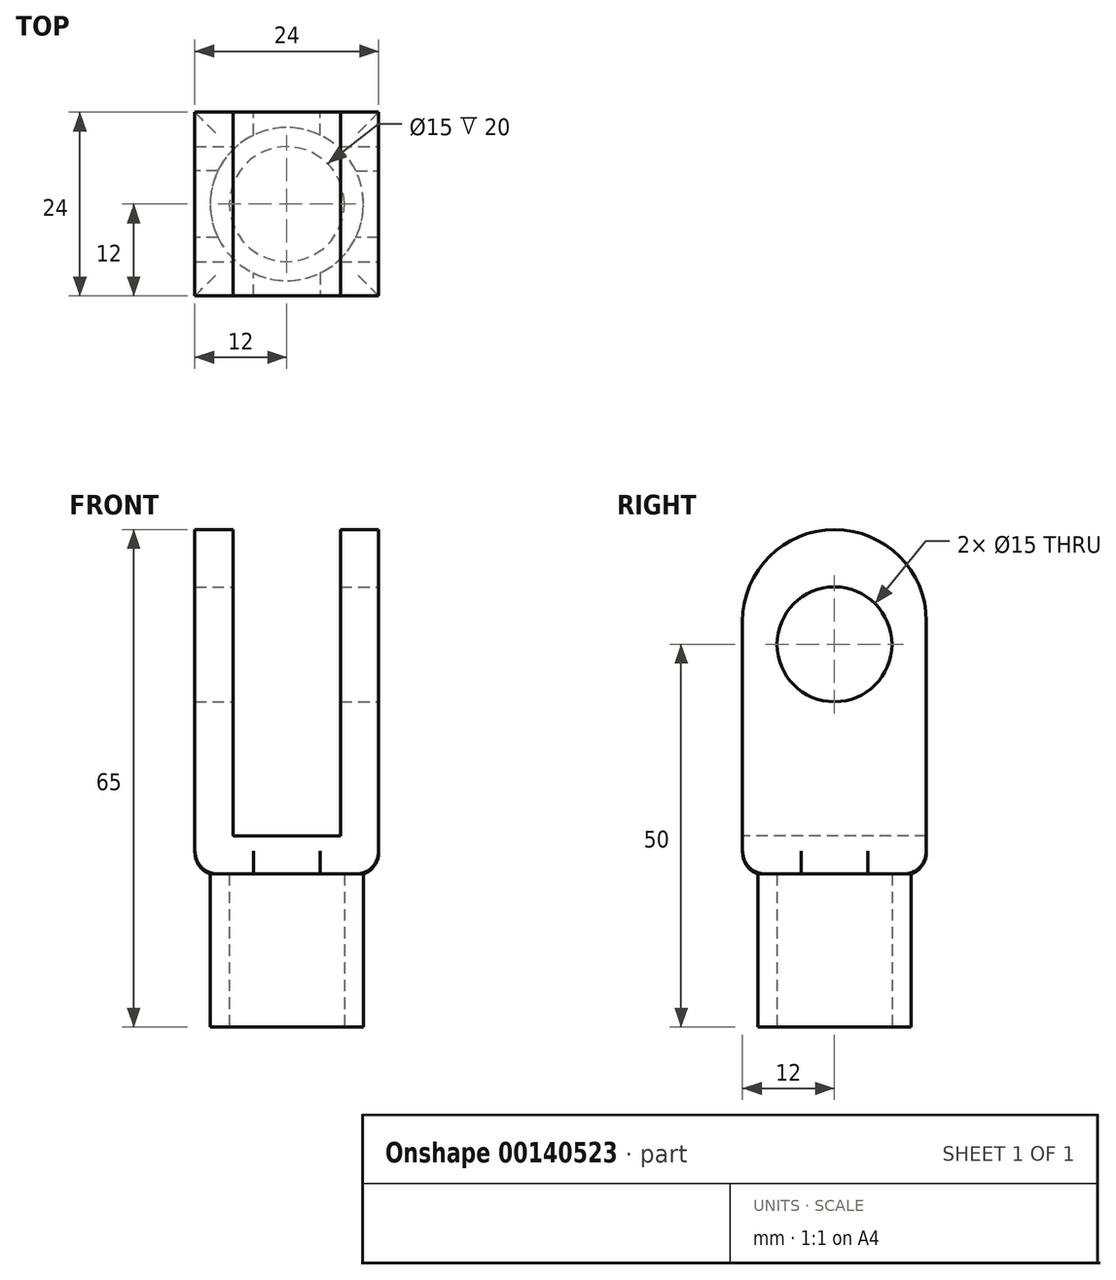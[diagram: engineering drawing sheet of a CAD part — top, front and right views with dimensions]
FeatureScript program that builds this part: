
annotation { "Feature Type Name" : "Feature", "Feature Type Description" : "" }
export const myFeature = defineFeature(function(context is Context, id is Id, definition is map)
    precondition{}
    {
        {
            var Q0;
            Q0=qCreatedBy(makeId("Top.planeOp"),FACE);
            var sketch = newSketch(context, id + "F0", { "sketchPlane" : qUnion([Q0])});
            skCircle(sketch, "E0", {"center": v(0, 0) * mm, "radius": 7.5 * mm});
            skCircle(sketch, "E1", {"center": v(0, 0) * mm, "radius": 10 * mm});
            skSolve(sketch);
        }
        {
            var Q0;
            Q0 = qSketchRegion(id + "F0", true);
            extrude(context, id + "F1", {"entities" : qUnion([Q0]), "depth" : 20 * mm});
        }
        {
            var Q0;
            Q0=makeQuery(id+"F1.opExtrude","CAP_FACE",FACE,{"disambiguationData":[OSD([sQuery(id+"F0.wireOp",EDGE,"E0"),sQuery(id+"F0.wireOp",EDGE,"E1")])],"isStart":false});
            var sketch = newSketch(context, id + "F2", { "sketchPlane" : qUnion([Q0])});
            skLineSegment(sketch, "E2.bottom", {"start": v(12, -12) * mm, "end": v(-12, -12) * mm});
            skLineSegment(sketch, "E2.top", {"start": v(12, 12) * mm, "end": v(-12, 12) * mm});
            skLineSegment(sketch, "E2.left", {"start": v(12, -12) * mm, "end": v(12, 12) * mm});
            skLineSegment(sketch, "E2.right", {"start": v(-12, -12) * mm, "end": v(-12, 12) * mm});
            skPoint(sketch, "E2.middle", {"position": v(0, 0) * mm});
            skSolve(sketch);
        }
        {
            var Q0;
            Q0 = qSketchRegion(id + "F2", true);
            extrude(context, id + "F3", {"entities" : qUnion([Q0]), "operationType" : NewBodyOperationType.ADD, "depth" : 5 * mm});
        }
        {
            var Q0;
            Q0=makeQuery(id+"F3.opExtrude","CAP_FACE",FACE,{"disambiguationData":[OSD([sQuery(id+"F2.wireOp",EDGE,"E2.bottom"),sQuery(id+"F2.wireOp",EDGE,"E2.top"),sQuery(id+"F2.wireOp",EDGE,"E2.left"),sQuery(id+"F2.wireOp",EDGE,"E2.right")])],"isStart":false});
            var sketch = newSketch(context, id + "F4", { "sketchPlane" : qUnion([Q0])});
            skLineSegment(sketch, "E3.bottom", {"start": v(-12, 12) * mm, "end": v(-7, 12) * mm});
            skLineSegment(sketch, "E3.top", {"start": v(-12, -12) * mm, "end": v(-7, -12) * mm});
            skLineSegment(sketch, "E3.left", {"start": v(-12, 12) * mm, "end": v(-12, -12) * mm});
            skLineSegment(sketch, "E3.right", {"start": v(-7, 12) * mm, "end": v(-7, -12) * mm});
            skLineSegment(sketch, "E4.bottom", {"start": v(12, 12) * mm, "end": v(7, 12) * mm});
            skLineSegment(sketch, "E4.top", {"start": v(12, -12) * mm, "end": v(7, -12) * mm});
            skLineSegment(sketch, "E4.left", {"start": v(12, 12) * mm, "end": v(12, -12) * mm});
            skLineSegment(sketch, "E4.right", {"start": v(7, 12) * mm, "end": v(7, -12) * mm});
            skSolve(sketch);
        }
        {
            var Q0;
            Q0 = qSketchRegion(id + "F4", true);
            extrude(context, id + "F5", {"entities" : qUnion([Q0]), "operationType" : NewBodyOperationType.ADD, "depth" : 40 * mm});
        }
        {
            var Q0;
            Q0=makeQuery(id+"F5.boolean.opBoolean","MERGE",FACE,{"derivedFrom":[makeQuery(id+"F3.opExtrude","SWEPT_FACE",FACE,{"disambiguationData":[OSD([sQuery(id+"F2.wireOp",EDGE,"E2.left")])]}),makeQuery(id+"F5.opExtrude","SWEPT_FACE",FACE,{"disambiguationData":[OSD([sQuery(id+"F4.wireOp",EDGE,"E4.left")])]})]});
            var sketch = newSketch(context, id + "F6", { "sketchPlane" : qUnion([Q0])});
            skCircle(sketch, "E5", {"center": v(0, 50) * mm, "radius": 7.5 * mm});
            skSolve(sketch);
        }
        {
            var Q0;
            Q0 = qSketchRegion(id + "F6", true);
            extrude(context, id + "F7", {"entities" : qUnion([Q0]), "operationType" : NewBodyOperationType.REMOVE, "endBound" : BoundingType.THROUGH_ALL, "oppositeDirection" : true, "depth" : 25 * mm});
        }
        {
            var Q0;
            Q0=makeQuery(id+"F5.opExtrude","CAP_EDGE",EDGE,{"disambiguationData":[OSD([sQuery(id+"F4.wireOp",EDGE,"E3.top")])],"isStart":false});
            var Q1;
            Q1=makeQuery(id+"F5.opExtrude","CAP_EDGE",EDGE,{"disambiguationData":[OSD([sQuery(id+"F4.wireOp",EDGE,"E3.bottom")])],"isStart":false});
            var Q2;
            Q2=makeQuery(id+"F5.opExtrude","CAP_EDGE",EDGE,{"disambiguationData":[OSD([sQuery(id+"F4.wireOp",EDGE,"E4.bottom")])],"isStart":false});
            var Q3;
            Q3=makeQuery(id+"F5.opExtrude","CAP_EDGE",EDGE,{"disambiguationData":[OSD([sQuery(id+"F4.wireOp",EDGE,"E4.top")])],"isStart":false});
            fillet(context, id + "F8", {"entities" : qUnion([Q0, Q1, Q2, Q3]), "radius" : 12 * mm, "tangentPropagation" : true, "allowEdgeOverflow" : false});
        }
        {
            var Q0;
            Q0=makeQuery(id+"F3.opExtrude","CAP_EDGE",EDGE,{"disambiguationData":[OSD([sQuery(id+"F2.wireOp",EDGE,"E2.left")])],"isStart":true});
            var Q1;
            Q1=makeQuery(id+"F3.opExtrude","CAP_EDGE",EDGE,{"disambiguationData":[OSD([sQuery(id+"F2.wireOp",EDGE,"E2.right")])],"isStart":true});
            var Q2;
            Q2=makeQuery(id+"F3.opExtrude","CAP_EDGE",EDGE,{"disambiguationData":[OSD([sQuery(id+"F2.wireOp",EDGE,"E2.bottom")])],"isStart":true});
            var Q3;
            Q3=makeQuery(id+"F3.opExtrude","CAP_EDGE",EDGE,{"disambiguationData":[OSD([sQuery(id+"F2.wireOp",EDGE,"E2.top")])],"isStart":true});
            fillet(context, id + "F9", {"entities" : qUnion([Q0, Q1, Q2, Q3]), "radius" : 3 * mm, "tangentPropagation" : true, "allowEdgeOverflow" : false});
        }
    });
